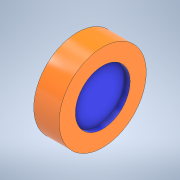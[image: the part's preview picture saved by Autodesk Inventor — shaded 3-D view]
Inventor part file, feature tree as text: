
AUTODESK INVENTOR PART (.ipt)
format: ipt  version: 2021 (Build 250183000, 183)  size: 121,856 bytes
history: native  units: mm
features: extrude x2, sketch x2
ambient origin geometry x8: Origin, YZ Plane, XZ Plane, XY Plane, X Axis, Y Axis, Z Axis, Center Point
bodies: Solid1 (feature_tree)
feature tree (4):
  extrude  "Extrusion1"  Depth=151.0mm
  extrude  "Extrusion2"  Depth=15.0mm
  sketch  "Sketch1"  dims[d0=240.0mm d1=151.0mm]
  sketch  "Sketch2"  dims[d2=70.0mm d3=0.0mm d4=151.0mm d5=15.0mm d6=0.0mm]
